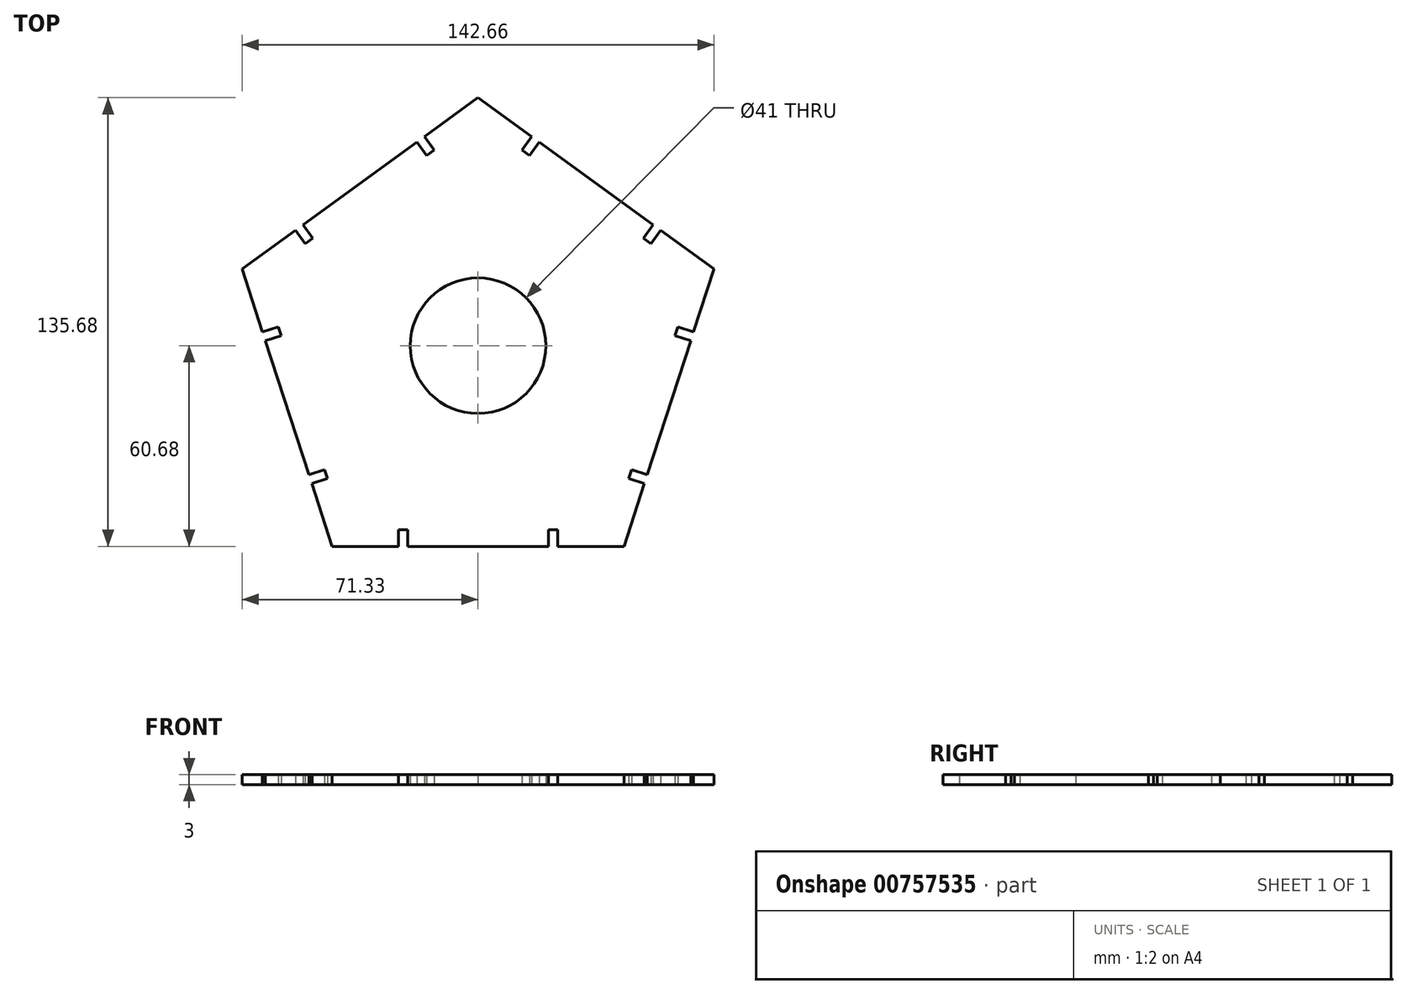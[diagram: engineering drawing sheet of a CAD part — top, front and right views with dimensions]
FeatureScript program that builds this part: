
annotation { "Feature Type Name" : "Feature", "Feature Type Description" : "" }
export const myFeature = defineFeature(function(context is Context, id is Id, definition is map)
    precondition{}
    {
        {
            var Q0;
            Q0=qCreatedBy(makeId("Top.planeOp"),FACE);
            var sketch = newSketch(context, id + "F0", { "sketchPlane" : qUnion([Q0])});
            skCircle(sketch, "E0.cCircle", {"center": v(0, 0) * mm, "radius": 75 * mm, "construction": true});
            skLineSegment(sketch, "E0.0", {"start": v(0, 75) * mm, "end": v(16.18, 63.24) * mm});
            skLineSegment(sketch, "E0.1", {"start": v(71.33, 23.18) * mm, "end": v(65.15, 4.16) * mm});
            skLineSegment(sketch, "E0.2", {"start": v(44.08, -60.68) * mm, "end": v(24.08, -60.68) * mm});
            skLineSegment(sketch, "E0.3", {"start": v(-44.08, -60.68) * mm, "end": v(-50.26, -41.66) * mm});
            skLineSegment(sketch, "E0.4", {"start": v(-71.33, 23.18) * mm, "end": v(-55.15, 34.93) * mm});
            skLineSegment(sketch, "E1", {"start": v(-16.18, 63.24) * mm, "end": v(-13.24, 59.2) * mm});
            skLineSegment(sketch, "E2", {"start": v(-13.24, 59.2) * mm, "end": v(-15.5, 57.55) * mm});
            skLineSegment(sketch, "E3", {"start": v(-15.5, 57.55) * mm, "end": v(-18.45, 61.6) * mm});
            skLineSegment(sketch, "E4", {"start": v(-35.66, 49.09) * mm, "end": v(44.08, -60.68) * mm, "construction": true});
            skLineSegment(sketch, "E5", {"start": v(-44.08, -60.68) * mm, "end": v(35.66, 49.09) * mm, "construction": true});
            skLineSegment(sketch, "E6", {"start": v(-71.33, 23.18) * mm, "end": v(57.7, -18.75) * mm, "construction": true});
            skLineSegment(sketch, "E7", {"start": v(71.33, 23.18) * mm, "end": v(-57.7, -18.75) * mm, "construction": true});
            skLineSegment(sketch, "E8", {"start": v(0, 75) * mm, "end": v(0, -60.68) * mm, "construction": true});
            skLineSegment(sketch, "E9.trimOffspring", {"start": v(-16.18, 63.24) * mm, "end": v(0, 75) * mm});
            skLineSegment(sketch, "E10.MirrorCS", {"start": v(-55.15, 34.93) * mm, "end": v(-52.2, 30.89) * mm});
            skLineSegment(sketch, "E11.MirrorCS", {"start": v(-49.94, 32.53) * mm, "end": v(-52.88, 36.58) * mm});
            skLineSegment(sketch, "E12.MirrorCS", {"start": v(-52.2, 30.89) * mm, "end": v(-49.94, 32.53) * mm});
            skLineSegment(sketch, "E13.trimOffspring", {"start": v(-52.88, 36.58) * mm, "end": v(-18.45, 61.6) * mm});
            skLineSegment(sketch, "E14.1.0", {"start": v(-65.15, 4.16) * mm, "end": v(-60.4, 5.7) * mm});
            skLineSegment(sketch, "E14.1.1", {"start": v(-59.53, 3.04) * mm, "end": v(-64.28, 1.5) * mm});
            skLineSegment(sketch, "E14.1.2", {"start": v(-60.4, 5.7) * mm, "end": v(-59.53, 3.04) * mm});
            skLineSegment(sketch, "E14.1.3", {"start": v(-46.37, -37.45) * mm, "end": v(-51.13, -39) * mm});
            skLineSegment(sketch, "E14.1.4", {"start": v(-45.5, -40.11) * mm, "end": v(-46.37, -37.45) * mm});
            skLineSegment(sketch, "E14.1.5", {"start": v(-50.26, -41.66) * mm, "end": v(-45.5, -40.11) * mm});
            skLineSegment(sketch, "E14.2.0", {"start": v(-24.08, -60.68) * mm, "end": v(-24.08, -55.68) * mm});
            skLineSegment(sketch, "E14.2.1", {"start": v(-21.28, -55.68) * mm, "end": v(-21.28, -60.68) * mm});
            skLineSegment(sketch, "E14.2.2", {"start": v(-24.08, -55.68) * mm, "end": v(-21.28, -55.68) * mm});
            skLineSegment(sketch, "E14.2.3", {"start": v(21.28, -55.68) * mm, "end": v(21.28, -60.68) * mm});
            skLineSegment(sketch, "E14.2.4", {"start": v(24.08, -55.68) * mm, "end": v(21.28, -55.68) * mm});
            skLineSegment(sketch, "E14.2.5", {"start": v(24.08, -60.68) * mm, "end": v(24.08, -55.68) * mm});
            skLineSegment(sketch, "E14.3.0", {"start": v(50.26, -41.66) * mm, "end": v(45.5, -40.11) * mm});
            skLineSegment(sketch, "E14.3.1", {"start": v(46.37, -37.45) * mm, "end": v(51.13, -39) * mm});
            skLineSegment(sketch, "E14.3.2", {"start": v(45.5, -40.11) * mm, "end": v(46.37, -37.45) * mm});
            skLineSegment(sketch, "E14.3.3", {"start": v(59.53, 3.04) * mm, "end": v(64.28, 1.5) * mm});
            skLineSegment(sketch, "E14.3.4", {"start": v(60.4, 5.7) * mm, "end": v(59.53, 3.04) * mm});
            skLineSegment(sketch, "E14.3.5", {"start": v(65.15, 4.16) * mm, "end": v(60.4, 5.7) * mm});
            skLineSegment(sketch, "E14.4.0", {"start": v(55.15, 34.93) * mm, "end": v(52.2, 30.89) * mm});
            skLineSegment(sketch, "E14.4.1", {"start": v(49.94, 32.53) * mm, "end": v(52.88, 36.58) * mm});
            skLineSegment(sketch, "E14.4.2", {"start": v(52.2, 30.89) * mm, "end": v(49.94, 32.53) * mm});
            skLineSegment(sketch, "E14.4.3", {"start": v(15.5, 57.55) * mm, "end": v(18.45, 61.6) * mm});
            skLineSegment(sketch, "E14.4.4", {"start": v(13.24, 59.2) * mm, "end": v(15.5, 57.55) * mm});
            skLineSegment(sketch, "E14.4.5", {"start": v(16.18, 63.24) * mm, "end": v(13.24, 59.2) * mm});
            skLineSegment(sketch, "E15.trimOffspring", {"start": v(-65.15, 4.16) * mm, "end": v(-71.33, 23.18) * mm});
            skLineSegment(sketch, "E16.trimOffspring", {"start": v(21.28, -60.68) * mm, "end": v(-21.28, -60.68) * mm});
            skLineSegment(sketch, "E17.trimOffspring", {"start": v(-24.08, -60.68) * mm, "end": v(-44.08, -60.68) * mm});
            skLineSegment(sketch, "E18.trimOffspring", {"start": v(-51.13, -39) * mm, "end": v(-64.28, 1.5) * mm});
            skLineSegment(sketch, "E19.trimOffspring", {"start": v(18.45, 61.6) * mm, "end": v(52.88, 36.58) * mm});
            skLineSegment(sketch, "E20.trimOffspring", {"start": v(55.15, 34.93) * mm, "end": v(71.33, 23.18) * mm});
            skLineSegment(sketch, "E21.trimOffspring", {"start": v(64.28, 1.5) * mm, "end": v(51.13, -39) * mm});
            skLineSegment(sketch, "E22.trimOffspring", {"start": v(50.26, -41.66) * mm, "end": v(44.08, -60.68) * mm});
            skCircle(sketch, "E23", {"center": v(0, 0) * mm, "radius": 20.5 * mm});
            skSolve(sketch);
        }
        {
            var Q0;
            Q0=qSketchRegion(id+"F0",true);
            extrude(context, id + "F1", {"entities" : qUnion([Q0]), "depth" : 3 * mm, "offsetDistance" : 25 * mm});
        }
    });
